# Revit family: VFH2-LH_DN50-150_RFA_1
name_source: partatom
category: Pipe Accessories
units: mm (PartAtom-declared; Revit-internal decimal feet)

## family parameters
Always vertical = Yes
Cut with Voids When Loaded = No
OmniClass Number = 23.65.55.14.17
OmniClass Title = Adjusting/Controlling Valves for Liquid Services
Part Type = Valve - Breaks Into
Round Connector Dimension = Use Diameter
Shared = No
Work Plane-Based = No

## types (6) — shared parameters
Connection = Lug
Description = Butterfly Valve
IfcExportAs = IfcValveType
IfcExportType = VFH2-LH
Manufacturer = Danfoss
Max Ambient Temperature = 60 °C
Max Differential Pressure = 16 bar
Max Medium Temperature = 95 °C
Min Ambient Temperature = -30 °C
Min Medium Temperature = -10 °C
Nominal Pressure = PN 16
URL = https://store.danfoss.com
Valve Body Material = Danfoss Cast Iron

## per-type parameters (varying)
- VFH2-LH_DN150_003Z5405: D=150 mm; D1=210 mm; D1_2=105 mm; D2_2=120 mm; D2_d1=280 mm; D3=90 mm; D4=106.05 mm; H=373 mm; H2=131 mm; Handle_Type=handle : 100-150; Kvs=1348.0 m³/h; L=113 mm; L1=53 mm; Model=003Z5405; Model Type=VFH2-LH_DN150; Operating Torque=95 Nm; W=390 mm; W1=131 mm; Weight=11.49 kg; a10=43.1 mm; a20=28 mm  [stored 0.0918635 ft]; a30=40 mm; a40=26 mm  [stored 0.0853018 ft]; a50=43.1 mm; ang1=7.50°; b10=13 mm; b20=43.5 mm; b30=12 mm  [stored 0.0393701 ft]; b40=40 mm; b50=43.5 mm; bt1=14 mm  [stored 0.0459318 ft]; d1=40 mm; d2=17 mm; h1=195 mm; h2=15 mm  [stored 0.0492126 ft]; h3=19 mm  [stored 0.062336 ft]; hb=14 mm  [stored 0.0459318 ft]; n=8; ofx=2.05 mm  [stored 0.00672572 ft]; ofy=9.1 mm  [stored 0.0298556 ft]; r1=100 mm; t1=59.6 mm; ta10=40 mm; ta20=26 mm  [stored 0.0853018 ft]; ta30=46 mm; ta40=29 mm  [stored 0.0951444 ft]; tb10=12 mm  [stored 0.0393701 ft]; tb20=40 mm; tb30=13 mm; tb40=45.5 mm; w1=45 mm
- VFH2-LH_DN125_003Z5404: D=125 mm; D1=189 mm; D1_2=94.5 mm; D2_2=105 mm; D2_d1=246 mm; D3=90 mm; D4=95.445 mm; H=345 mm; H2=115 mm; Handle_Type=handle : 100-150; Kvs=874.0 m³/h; L=113 mm; L1=53 mm; Model=003Z5404; Model Type=VFH2-LH_DN125; Operating Torque=68 Nm; W=375 mm; W1=115 mm; Weight=9.99 kg; a10=43.1 mm; a20=28 mm  [stored 0.0918635 ft]; a30=40 mm; a40=26 mm  [stored 0.0853018 ft]; a50=43.1 mm; ang1=7.50°; b10=13 mm; b20=43.5 mm; b30=12 mm  [stored 0.0393701 ft]; b40=40 mm; b50=43.5 mm; bt1=14 mm  [stored 0.0459318 ft]; d1=36 mm  [stored 0.11811 ft]; d2=14 mm  [stored 0.0459318 ft]; h1=182 mm; h2=15 mm  [stored 0.0492126 ft]; h3=19 mm  [stored 0.062336 ft]; hb=11.5 mm  [stored 0.0377297 ft]; n=8; ofx=2.05 mm  [stored 0.00672572 ft]; ofy=11.4 mm  [stored 0.0374016 ft]; r1=89.5 mm; t1=59.6 mm; ta10=40 mm; ta20=26 mm  [stored 0.0853018 ft]; ta30=48 mm; ta40=31 mm  [stored 0.101706 ft]; tb10=12 mm  [stored 0.0393701 ft]; tb20=40 mm; tb30=13 mm; tb40=48 mm; w1=42 mm
- VFH2-LH_DN100_003Z5403: D=100 mm; D1=157 mm; D1_2=78.5 mm; D2_2=90 mm; D2_d1=216 mm; D3=90 mm; D4=79.285 mm; H=315 mm; H2=102 mm; Handle_Type=handle : 100-150; Kvs=569.0 m³/h; L=113 mm; L1=53 mm; Model=003Z5403; Model Type=VFH2-LH_DN100; Operating Torque=46 Nm; W=362 mm; W1=102 mm; Weight=7.73 kg; a10=37 mm  [stored 0.121391 ft]; a20=28 mm  [stored 0.0918635 ft]; a30=34 mm  [stored 0.111549 ft]; a40=26 mm  [stored 0.0853018 ft]; a50=37 mm  [stored 0.121391 ft]; ang1=7.50°; b10=12.6 mm  [stored 0.0413386 ft]; b20=37.2 mm; b30=12 mm  [stored 0.0393701 ft]; b40=34 mm  [stored 0.111549 ft]; b50=37.2 mm; bt1=11 mm  [stored 0.0360892 ft]; d1=36 mm  [stored 0.11811 ft]; d2=14 mm  [stored 0.0459318 ft]; h1=168 mm; h2=13 mm; h3=17 mm; hb=16.5 mm  [stored 0.0541339 ft]; n=8; ofx=2.05 mm  [stored 0.00672572 ft]; ofy=7.75 mm  [stored 0.0254265 ft]; r1=73.5 mm; t1=55.6 mm; ta10=34 mm  [stored 0.111549 ft]; ta20=26 mm  [stored 0.0853018 ft]; ta30=43.5 mm; ta40=32 mm  [stored 0.104987 ft]; tb10=11.6 mm  [stored 0.0380577 ft]; tb20=34 mm  [stored 0.111549 ft]; tb30=13 mm; tb40=43 mm; w1=36 mm  [stored 0.11811 ft]
- VFH2-LH_DN80_003Z5402: D=80 mm; D1=126 mm; D1_2=63 mm; D2_2=80 mm; D2_d1=196 mm; D3=65 mm; D4=63.63 mm; H=285 mm; H2=92 mm; Handle_Type=handle : 32-80; Kvs=288.0 m³/h; L=76 mm; L1=36 mm  [stored 0.11811 ft]; Model=003Z5402; Model Type=VFH2-LH_DN80; Operating Torque=29 Nm; W=287 mm; W1=92 mm; Weight=6.25 kg; a10=37 mm  [stored 0.121391 ft]; a20=22 mm  [stored 0.0721785 ft]; a30=32 mm  [stored 0.104987 ft]; a40=20 mm  [stored 0.0656168 ft]; a50=37 mm  [stored 0.121391 ft]; ang1=7.50°; b10=12.9 mm  [stored 0.0423228 ft]; b20=37.2 mm; b30=13 mm; b40=34 mm  [stored 0.111549 ft]; b50=37.2 mm; bt1=9 mm  [stored 0.0295276 ft]; d1=36 mm  [stored 0.11811 ft]; d2=14 mm  [stored 0.0459318 ft]; h1=150 mm; h2=12 mm  [stored 0.0393701 ft]; h3=17 mm; hb=14 mm  [stored 0.0459318 ft]; n=8; ofx=2 mm  [stored 0.00656168 ft]; ofy=5 mm  [stored 0.0164042 ft]; r1=58 mm; t1=49.6 mm; ta10=34 mm  [stored 0.111549 ft]; ta20=20 mm  [stored 0.0656168 ft]; ta30=36 mm  [stored 0.11811 ft]; ta40=21 mm  [stored 0.0688976 ft]; tb10=11.4 mm  [stored 0.0374016 ft]; tb20=34 mm  [stored 0.111549 ft]; tb30=13 mm; tb40=36.5 mm  [stored 0.119751 ft]; w1=35 mm  [stored 0.114829 ft]
- VFH2-LH_DN65_003Z5401: D=65 mm; D1=107 mm; D1_2=53.5 mm; D2_2=72.5 mm; D2_d1=181 mm; D3=65 mm; D4=54.035 mm; H=255 mm; H2=70 mm; Handle_Type=handle : 32-80; Kvs=207.0 m³/h; L=76 mm; L1=36 mm  [stored 0.11811 ft]; Model=003Z5401; Model Type=VFH2-LH_DN65; Operating Torque=23 Nm; W=265 mm; W1=70 mm; Weight=4.00 kg; a10=35 mm  [stored 0.114829 ft]; a20=23 mm  [stored 0.0754593 ft]; a30=34 mm  [stored 0.111549 ft]; a40=25 mm  [stored 0.082021 ft]; a50=35 mm  [stored 0.114829 ft]; ang1=75.00°; b10=16 mm  [stored 0.0524934 ft]; b20=37 mm  [stored 0.121391 ft]; b30=15 mm  [stored 0.0492126 ft]; b40=34.4 mm; b50=37 mm  [stored 0.121391 ft]; bt1=9 mm  [stored 0.0295276 ft]; d1=36 mm  [stored 0.11811 ft]; d2=14 mm  [stored 0.0459318 ft]; h1=143 mm; h2=12 mm  [stored 0.0393701 ft]; h3=17 mm; hb=18 mm  [stored 0.0590551 ft]; n=4; ofx=2 mm  [stored 0.00656168 ft]; ofy=5 mm  [stored 0.0164042 ft]; r1=48.5 mm; t1=49.6 mm; ta10=32 mm  [stored 0.104987 ft]; ta20=21 mm  [stored 0.0688976 ft]; ta30=36 mm  [stored 0.11811 ft]; ta40=26 mm  [stored 0.0853018 ft]; tb10=15 mm  [stored 0.0492126 ft]; tb20=34 mm  [stored 0.111549 ft]; tb30=15.3 mm  [stored 0.0501969 ft]; tb40=35 mm  [stored 0.114829 ft]; w1=30 mm  [stored 0.0984252 ft]
- VFH2-LH_DN50_003Z5400: D=50 mm; D1=94 mm; D1_2=47 mm; D2_2=62.5 mm; D2_d1=161 mm; D3=65 mm; D4=47.47 mm; H=235 mm; H2=62 mm; Handle_Type=handle : 32-80; Kvs=82.0 m³/h; L=76 mm; L1=36 mm  [stored 0.11811 ft]; Model=003Z5400; Model Type=VFH2-LH_DN50; Operating Torque=15 Nm; W=258 mm; W1=63 mm; Weight=3.19 kg; a10=33.5 mm  [stored 0.109908 ft]; a20=23 mm  [stored 0.0754593 ft]; a30=34 mm  [stored 0.111549 ft]; a40=25 mm  [stored 0.082021 ft]; a50=33.5 mm  [stored 0.109908 ft]; ang1=75.00°; b10=16 mm  [stored 0.0524934 ft]; b20=37 mm  [stored 0.121391 ft]; b30=15 mm  [stored 0.0492126 ft]; b40=34.4 mm; b50=37 mm  [stored 0.121391 ft]; bt1=9 mm  [stored 0.0295276 ft]; d1=36 mm  [stored 0.11811 ft]; d2=14 mm  [stored 0.0459318 ft]; h1=131 mm; h2=12 mm  [stored 0.0393701 ft]; h3=17 mm; hb=13 mm; n=4; ofx=2 mm  [stored 0.00656168 ft]; ofy=5 mm  [stored 0.0164042 ft]; r1=42 mm; t1=46.6 mm; ta10=30 mm  [stored 0.0984252 ft]; ta20=22 mm  [stored 0.0721785 ft]; ta30=36 mm  [stored 0.11811 ft]; ta40=26 mm  [stored 0.0853018 ft]; tb10=15 mm  [stored 0.0492126 ft]; tb20=34 mm  [stored 0.111549 ft]; tb30=15.3 mm  [stored 0.0501969 ft]; tb40=35 mm  [stored 0.114829 ft]; w1=30 mm  [stored 0.0984252 ft]

note: [stored X ft] marks values corroborated as IEEE doubles in the binary element streams (Revit-internal decimal feet)

## geometry (parser evidence)
native form markers: Blend x2, Sweep x12
no freeform markers — native parametric forms only
